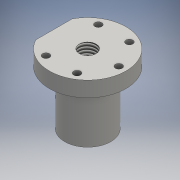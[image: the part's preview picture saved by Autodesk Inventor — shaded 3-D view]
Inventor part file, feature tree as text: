
AUTODESK INVENTOR PART (.ipt)
format: ipt  version: 2016 (Build 200138000, 138)  size: 182,272 bytes
history: native  units: mm
features: sketch x7, extrude x6, revolve x1, thread x1, plane x1
ambient origin geometry x8: Origin, YZ Plane, XZ Plane, XY Plane, X Axis, Y Axis, Z Axis, Center Point
bodies: Solid1 (feature_tree)
feature tree (16):
  revolve  "Revolution1"  [1 undecoded]
  extrude  "Extrusion1"  Depth=10.0mm
  extrude  "Extrusion2"  TaperAngle=90.0deg  [1 undecoded]
  thread  "Thread1"  [1 undecoded]
  extrude  "Extrusion3"  Depth=10.0mm TaperAngle=0.0deg
  plane  "Work Plane1"
  extrude  "Extrusion4"  Depth=10.0mm TaperAngle=0.0deg
  extrude  "Extrusion5"  Depth=10.0mm TaperAngle=0.0deg
  extrude  "Extrusion8"  Depth=10.0mm
  sketch  "Sketch1"  dims[d3=25.0mm d4=10.0mm]
  sketch  "Sketch2"  dims[d5=10.0mm d6=35.0mm]
  sketch  "Sketch3"  dims[d7=15.0mm d8=90.0deg d12=4.5mm]
  sketch  "Sketch4"  dims[d13=60.0mm d15=360.0deg d17=10.0mm d18=0.0mm]
  sketch  "Sketch5"  dims[d19=11.0mm d27=10.0mm d28=0.0mm]
  sketch  "Sketch9"  dims[d29=10.0mm d30=0.0mm d32=15.0mm d33=0.0mm]
  sketch  "Sketch20"  dims[d37=1.0mm d38=0.0mm d59=8.0mm d60=10.0mm d61=0.0mm d76=18.0mm d77=6.0mm d78=9.25mm d79=9.25mm d80=7.5mm d81=2.0mm d82=2.0mm d83=4.75mm d84=0.0mm]
note: 3 required parameter values undecoded (feature->parameter linkage not recoverable at this tier; creation-order binding heuristic only, values carry confidence <= 0.55)